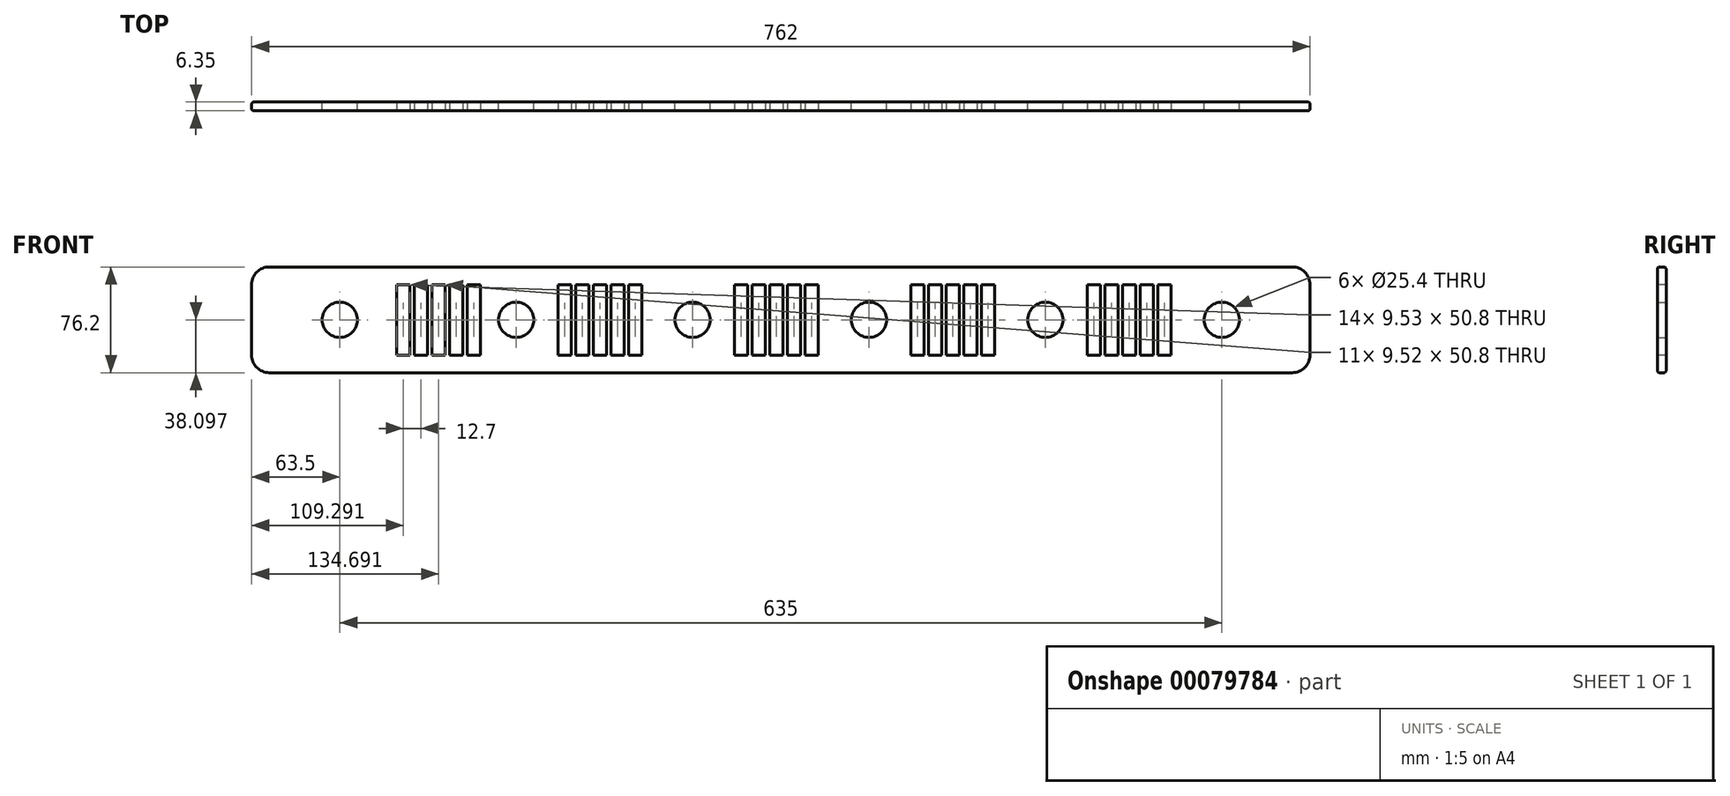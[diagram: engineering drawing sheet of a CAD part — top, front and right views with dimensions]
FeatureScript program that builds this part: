
annotation { "Feature Type Name" : "Feature", "Feature Type Description" : "" }
export const myFeature = defineFeature(function(context is Context, id is Id, definition is map)
    precondition{}
    {
        {
            var Q0;
            Q0=qCreatedBy(makeId("Front.planeOp"),FACE);
            var sketch = newSketch(context, id + "F0", { "sketchPlane" : qUnion([Q0])});
            skLineSegment(sketch, "E0.bottom", {"start": v(-190.5, 22.29) * mm, "end": v(571.5, 22.29) * mm});
            skLineSegment(sketch, "E0.top", {"start": v(-190.5, -53.91) * mm, "end": v(571.5, -53.91) * mm});
            skLineSegment(sketch, "E0.left", {"start": v(-190.5, 22.29) * mm, "end": v(-190.5, -53.91) * mm});
            skLineSegment(sketch, "E0.right", {"start": v(571.5, 22.29) * mm, "end": v(571.5, -53.91) * mm});
            skCircle(sketch, "E1", {"center": v(-127, -15.81) * mm, "radius": 12.7 * mm});
            skPoint(sketch, "E1.centerSnap0", {"position": v(-190.5, -15.81) * mm});
            skCircle(sketch, "E2", {"center": v(0, -15.81) * mm, "radius": 12.7 * mm});
            skCircle(sketch, "E3", {"center": v(127, -15.81) * mm, "radius": 12.7 * mm});
            skCircle(sketch, "E4", {"center": v(254, -15.81) * mm, "radius": 12.7 * mm});
            skCircle(sketch, "E5", {"center": v(381, -15.81) * mm, "radius": 12.7 * mm});
            skCircle(sketch, "E6", {"center": v(508, -15.81) * mm, "radius": 12.7 * mm});
            skSolve(sketch);
        }
        {
            var Q0;
            Q0=makeQuery(id+"F0.imprint","IMPRINT",FACE,{"disambiguationData":[TD([[makeQuery(id+"F0.imprint","IMPRINT",EDGE,{"derivedFrom":sQuery(id+"F0.wireOp",EDGE,"E0.bottom")}),-1.0]])]});
            extrude(context, id + "F1", {"entities" : qUnion([Q0]), "depth" : 6.35 * mm});
        }
        {
            var Q0;
            Q0=makeQuery(id+"F1.opExtrude","CAP_FACE",FACE,{"disambiguationData":[OSD([sQuery(id+"F0.wireOp",EDGE,"E0.bottom"),sQuery(id+"F0.wireOp",EDGE,"E0.top"),sQuery(id+"F0.wireOp",EDGE,"E0.left"),sQuery(id+"F0.wireOp",EDGE,"E0.right"),sQuery(id+"F0.wireOp",EDGE,"E1"),sQuery(id+"F0.wireOp",EDGE,"E2"),sQuery(id+"F0.wireOp",EDGE,"E3"),sQuery(id+"F0.wireOp",EDGE,"E4"),sQuery(id+"F0.wireOp",EDGE,"E5"),sQuery(id+"F0.wireOp",EDGE,"E6")])],"isStart":false});
            var sketch = newSketch(context, id + "F2", { "sketchPlane" : qUnion([Q0])});
            skLineSegment(sketch, "E7.bottom", {"start": v(30.18, 9.59) * mm, "end": v(39.7, 9.59) * mm});
            skLineSegment(sketch, "E7.top", {"start": v(30.18, -41.21) * mm, "end": v(39.7, -41.21) * mm});
            skLineSegment(sketch, "E7.left", {"start": v(30.18, 9.59) * mm, "end": v(30.18, -41.21) * mm});
            skLineSegment(sketch, "E7.right", {"start": v(39.7, 9.59) * mm, "end": v(39.7, -41.21) * mm});
            skLineSegment(sketch, "E8.1.0.0", {"start": v(42.88, 9.59) * mm, "end": v(42.88, -41.21) * mm});
            skLineSegment(sketch, "E8.1.0.1", {"start": v(52.4, 9.59) * mm, "end": v(52.4, -41.21) * mm});
            skLineSegment(sketch, "E8.1.0.2", {"start": v(42.88, -41.21) * mm, "end": v(52.4, -41.21) * mm});
            skLineSegment(sketch, "E8.1.0.3", {"start": v(42.88, 9.59) * mm, "end": v(52.4, 9.59) * mm});
            skLineSegment(sketch, "E8.2.0.0", {"start": v(55.58, 9.59) * mm, "end": v(55.58, -41.21) * mm});
            skLineSegment(sketch, "E8.2.0.1", {"start": v(65.1, 9.59) * mm, "end": v(65.1, -41.21) * mm});
            skLineSegment(sketch, "E8.2.0.2", {"start": v(55.58, -41.21) * mm, "end": v(65.1, -41.21) * mm});
            skLineSegment(sketch, "E8.2.0.3", {"start": v(55.58, 9.59) * mm, "end": v(65.1, 9.59) * mm});
            skLineSegment(sketch, "E8.3.0.0", {"start": v(68.28, 9.59) * mm, "end": v(68.28, -41.21) * mm});
            skLineSegment(sketch, "E8.3.0.1", {"start": v(77.8, 9.59) * mm, "end": v(77.8, -41.21) * mm});
            skLineSegment(sketch, "E8.3.0.2", {"start": v(68.28, -41.21) * mm, "end": v(77.8, -41.21) * mm});
            skLineSegment(sketch, "E8.3.0.3", {"start": v(68.28, 9.59) * mm, "end": v(77.8, 9.59) * mm});
            skLineSegment(sketch, "E8.4.0.0", {"start": v(80.98, 9.59) * mm, "end": v(80.98, -41.21) * mm});
            skLineSegment(sketch, "E8.4.0.1", {"start": v(90.5, 9.59) * mm, "end": v(90.5, -41.21) * mm});
            skLineSegment(sketch, "E8.4.0.2", {"start": v(80.98, -41.21) * mm, "end": v(90.5, -41.21) * mm});
            skLineSegment(sketch, "E8.4.0.3", {"start": v(80.98, 9.59) * mm, "end": v(90.5, 9.59) * mm});
            skLineSegment(sketch, "E8.direction1", {"start": v(30.18, -41.21) * mm, "end": v(42.88, -41.21) * mm, "construction": true});
            skLineSegment(sketch, "E9.bottom", {"start": v(157.18, 9.59) * mm, "end": v(166.7, 9.59) * mm});
            skLineSegment(sketch, "E9.top", {"start": v(157.18, -41.21) * mm, "end": v(166.7, -41.21) * mm});
            skLineSegment(sketch, "E9.left", {"start": v(157.18, 9.59) * mm, "end": v(157.18, -41.21) * mm});
            skLineSegment(sketch, "E9.right", {"start": v(166.7, 9.59) * mm, "end": v(166.7, -41.21) * mm});
            skLineSegment(sketch, "E10.1.0.0", {"start": v(169.88, 9.59) * mm, "end": v(169.88, -41.21) * mm});
            skLineSegment(sketch, "E10.1.0.1", {"start": v(179.4, 9.59) * mm, "end": v(179.4, -41.21) * mm});
            skLineSegment(sketch, "E10.1.0.2", {"start": v(169.88, -41.21) * mm, "end": v(179.4, -41.21) * mm});
            skLineSegment(sketch, "E10.1.0.3", {"start": v(169.88, 9.59) * mm, "end": v(179.4, 9.59) * mm});
            skLineSegment(sketch, "E10.2.0.0", {"start": v(182.58, 9.59) * mm, "end": v(182.58, -41.21) * mm});
            skLineSegment(sketch, "E10.2.0.1", {"start": v(192.1, 9.59) * mm, "end": v(192.1, -41.21) * mm});
            skLineSegment(sketch, "E10.2.0.2", {"start": v(182.58, -41.21) * mm, "end": v(192.1, -41.21) * mm});
            skLineSegment(sketch, "E10.2.0.3", {"start": v(182.58, 9.59) * mm, "end": v(192.1, 9.59) * mm});
            skLineSegment(sketch, "E10.3.0.0", {"start": v(195.28, 9.59) * mm, "end": v(195.28, -41.21) * mm});
            skLineSegment(sketch, "E10.3.0.1", {"start": v(204.8, 9.59) * mm, "end": v(204.8, -41.21) * mm});
            skLineSegment(sketch, "E10.3.0.2", {"start": v(195.28, -41.21) * mm, "end": v(204.8, -41.21) * mm});
            skLineSegment(sketch, "E10.3.0.3", {"start": v(195.28, 9.59) * mm, "end": v(204.8, 9.59) * mm});
            skLineSegment(sketch, "E10.4.0.0", {"start": v(207.98, 9.59) * mm, "end": v(207.98, -41.21) * mm});
            skLineSegment(sketch, "E10.4.0.1", {"start": v(217.5, 9.59) * mm, "end": v(217.5, -41.21) * mm});
            skLineSegment(sketch, "E10.4.0.2", {"start": v(207.98, -41.21) * mm, "end": v(217.5, -41.21) * mm});
            skLineSegment(sketch, "E10.4.0.3", {"start": v(207.98, 9.59) * mm, "end": v(217.5, 9.59) * mm});
            skLineSegment(sketch, "E10.direction1", {"start": v(157.18, -41.21) * mm, "end": v(169.88, -41.21) * mm, "construction": true});
            skLineSegment(sketch, "E11.bottom", {"start": v(284.18, 9.59) * mm, "end": v(293.7, 9.59) * mm});
            skLineSegment(sketch, "E11.top", {"start": v(284.18, -41.21) * mm, "end": v(293.7, -41.21) * mm});
            skLineSegment(sketch, "E11.left", {"start": v(284.18, 9.59) * mm, "end": v(284.18, -41.21) * mm});
            skLineSegment(sketch, "E11.right", {"start": v(293.7, 9.59) * mm, "end": v(293.7, -41.21) * mm});
            skLineSegment(sketch, "E12.1.0.0", {"start": v(296.88, 9.59) * mm, "end": v(296.88, -41.21) * mm});
            skLineSegment(sketch, "E12.1.0.1", {"start": v(306.4, 9.59) * mm, "end": v(306.4, -41.21) * mm});
            skLineSegment(sketch, "E12.1.0.2", {"start": v(296.88, -41.21) * mm, "end": v(306.4, -41.21) * mm});
            skLineSegment(sketch, "E12.1.0.3", {"start": v(296.88, 9.59) * mm, "end": v(306.4, 9.59) * mm});
            skLineSegment(sketch, "E12.2.0.0", {"start": v(309.58, 9.59) * mm, "end": v(309.58, -41.21) * mm});
            skLineSegment(sketch, "E12.2.0.1", {"start": v(319.1, 9.59) * mm, "end": v(319.1, -41.21) * mm});
            skLineSegment(sketch, "E12.2.0.2", {"start": v(309.58, -41.21) * mm, "end": v(319.1, -41.21) * mm});
            skLineSegment(sketch, "E12.2.0.3", {"start": v(309.58, 9.59) * mm, "end": v(319.1, 9.59) * mm});
            skLineSegment(sketch, "E12.3.0.0", {"start": v(322.28, 9.59) * mm, "end": v(322.28, -41.21) * mm});
            skLineSegment(sketch, "E12.3.0.1", {"start": v(331.8, 9.59) * mm, "end": v(331.8, -41.21) * mm});
            skLineSegment(sketch, "E12.3.0.2", {"start": v(322.28, -41.21) * mm, "end": v(331.8, -41.21) * mm});
            skLineSegment(sketch, "E12.3.0.3", {"start": v(322.28, 9.59) * mm, "end": v(331.8, 9.59) * mm});
            skLineSegment(sketch, "E12.4.0.0", {"start": v(334.98, 9.59) * mm, "end": v(334.98, -41.21) * mm});
            skLineSegment(sketch, "E12.4.0.1", {"start": v(344.5, 9.59) * mm, "end": v(344.5, -41.21) * mm});
            skLineSegment(sketch, "E12.4.0.2", {"start": v(334.98, -41.21) * mm, "end": v(344.5, -41.21) * mm});
            skLineSegment(sketch, "E12.4.0.3", {"start": v(334.98, 9.59) * mm, "end": v(344.5, 9.59) * mm});
            skLineSegment(sketch, "E12.direction1", {"start": v(284.18, -41.21) * mm, "end": v(296.88, -41.21) * mm, "construction": true});
            skLineSegment(sketch, "E13.bottom", {"start": v(411.18, 9.59) * mm, "end": v(420.7, 9.59) * mm});
            skLineSegment(sketch, "E13.top", {"start": v(411.18, -41.21) * mm, "end": v(420.7, -41.21) * mm});
            skLineSegment(sketch, "E13.left", {"start": v(411.18, 9.59) * mm, "end": v(411.18, -41.21) * mm});
            skLineSegment(sketch, "E13.right", {"start": v(420.7, 9.59) * mm, "end": v(420.7, -41.21) * mm});
            skLineSegment(sketch, "E14.1.0.0", {"start": v(423.88, 9.59) * mm, "end": v(423.88, -41.21) * mm});
            skLineSegment(sketch, "E14.1.0.1", {"start": v(433.4, 9.59) * mm, "end": v(433.4, -41.21) * mm});
            skLineSegment(sketch, "E14.1.0.2", {"start": v(423.88, -41.21) * mm, "end": v(433.4, -41.21) * mm});
            skLineSegment(sketch, "E14.1.0.3", {"start": v(423.88, 9.59) * mm, "end": v(433.4, 9.59) * mm});
            skLineSegment(sketch, "E14.2.0.0", {"start": v(436.58, 9.59) * mm, "end": v(436.58, -41.21) * mm});
            skLineSegment(sketch, "E14.2.0.1", {"start": v(446.1, 9.59) * mm, "end": v(446.1, -41.21) * mm});
            skLineSegment(sketch, "E14.2.0.2", {"start": v(436.58, -41.21) * mm, "end": v(446.1, -41.21) * mm});
            skLineSegment(sketch, "E14.2.0.3", {"start": v(436.58, 9.59) * mm, "end": v(446.1, 9.59) * mm});
            skLineSegment(sketch, "E14.3.0.0", {"start": v(449.28, 9.59) * mm, "end": v(449.28, -41.21) * mm});
            skLineSegment(sketch, "E14.3.0.1", {"start": v(458.8, 9.59) * mm, "end": v(458.8, -41.21) * mm});
            skLineSegment(sketch, "E14.3.0.2", {"start": v(449.28, -41.21) * mm, "end": v(458.8, -41.21) * mm});
            skLineSegment(sketch, "E14.3.0.3", {"start": v(449.28, 9.59) * mm, "end": v(458.8, 9.59) * mm});
            skLineSegment(sketch, "E14.4.0.0", {"start": v(461.98, 9.59) * mm, "end": v(461.98, -41.21) * mm});
            skLineSegment(sketch, "E14.4.0.1", {"start": v(471.5, 9.59) * mm, "end": v(471.5, -41.21) * mm});
            skLineSegment(sketch, "E14.4.0.2", {"start": v(461.98, -41.21) * mm, "end": v(471.5, -41.21) * mm});
            skLineSegment(sketch, "E14.4.0.3", {"start": v(461.98, 9.59) * mm, "end": v(471.5, 9.59) * mm});
            skLineSegment(sketch, "E14.direction1", {"start": v(411.18, -41.21) * mm, "end": v(423.88, -41.21) * mm, "construction": true});
            skLineSegment(sketch, "E15.bottom", {"start": v(-85.97, 9.59) * mm, "end": v(-76.45, 9.59) * mm});
            skLineSegment(sketch, "E15.top", {"start": v(-85.97, -41.21) * mm, "end": v(-76.45, -41.21) * mm});
            skLineSegment(sketch, "E15.left", {"start": v(-85.97, 9.59) * mm, "end": v(-85.97, -41.21) * mm});
            skLineSegment(sketch, "E15.right", {"start": v(-76.45, 9.59) * mm, "end": v(-76.45, -41.21) * mm});
            skLineSegment(sketch, "E16.1.0.0", {"start": v(-73.27, 9.59) * mm, "end": v(-73.27, -41.21) * mm});
            skLineSegment(sketch, "E16.1.0.1", {"start": v(-63.75, 9.59) * mm, "end": v(-63.75, -41.21) * mm});
            skLineSegment(sketch, "E16.1.0.2", {"start": v(-73.27, -41.21) * mm, "end": v(-63.75, -41.21) * mm});
            skLineSegment(sketch, "E16.1.0.3", {"start": v(-73.27, 9.59) * mm, "end": v(-63.75, 9.59) * mm});
            skLineSegment(sketch, "E16.2.0.0", {"start": v(-60.57, 9.59) * mm, "end": v(-60.57, -41.21) * mm});
            skLineSegment(sketch, "E16.2.0.1", {"start": v(-51.05, 9.59) * mm, "end": v(-51.05, -41.21) * mm});
            skLineSegment(sketch, "E16.2.0.2", {"start": v(-60.57, -41.21) * mm, "end": v(-51.05, -41.21) * mm});
            skLineSegment(sketch, "E16.2.0.3", {"start": v(-60.57, 9.59) * mm, "end": v(-51.05, 9.59) * mm});
            skLineSegment(sketch, "E16.3.0.0", {"start": v(-47.87, 9.59) * mm, "end": v(-47.87, -41.21) * mm});
            skLineSegment(sketch, "E16.3.0.1", {"start": v(-38.35, 9.59) * mm, "end": v(-38.35, -41.21) * mm});
            skLineSegment(sketch, "E16.3.0.2", {"start": v(-47.87, -41.21) * mm, "end": v(-38.35, -41.21) * mm});
            skLineSegment(sketch, "E16.3.0.3", {"start": v(-47.87, 9.59) * mm, "end": v(-38.35, 9.59) * mm});
            skLineSegment(sketch, "E16.4.0.0", {"start": v(-35.17, 9.59) * mm, "end": v(-35.17, -41.21) * mm});
            skLineSegment(sketch, "E16.4.0.1", {"start": v(-25.65, 9.59) * mm, "end": v(-25.65, -41.21) * mm});
            skLineSegment(sketch, "E16.4.0.2", {"start": v(-35.17, -41.21) * mm, "end": v(-25.65, -41.21) * mm});
            skLineSegment(sketch, "E16.4.0.3", {"start": v(-35.17, 9.59) * mm, "end": v(-25.65, 9.59) * mm});
            skLineSegment(sketch, "E16.direction1", {"start": v(-85.97, -41.21) * mm, "end": v(-73.27, -41.21) * mm, "construction": true});
            skSolve(sketch);
        }
        {
            var Q0;
            Q0 = qSketchRegion(id + "F2", true);
            extrude(context, id + "F3", {"entities" : qUnion([Q0]), "operationType" : NewBodyOperationType.REMOVE, "oppositeDirection" : true, "depth" : 25.4 * mm});
        }
        {
            var Q0;
            Q0=makeQuery(id+"F1.opExtrude","SWEPT_EDGE",EDGE,{"disambiguationData":[OSD([sQuery(id+"F0.wireOp",EDGE,"E0.bottom"),sQuery(id+"F0.wireOp",EDGE,"E0.left")])]});
            var Q1;
            Q1=makeQuery(id+"F1.opExtrude","SWEPT_EDGE",EDGE,{"disambiguationData":[OSD([sQuery(id+"F0.wireOp",EDGE,"E0.top"),sQuery(id+"F0.wireOp",EDGE,"E0.left")])]});
            var Q2;
            Q2=makeQuery(id+"F1.opExtrude","SWEPT_EDGE",EDGE,{"disambiguationData":[OSD([sQuery(id+"F0.wireOp",EDGE,"E0.bottom"),sQuery(id+"F0.wireOp",EDGE,"E0.right")])]});
            var Q3;
            Q3=makeQuery(id+"F1.opExtrude","SWEPT_EDGE",EDGE,{"disambiguationData":[OSD([sQuery(id+"F0.wireOp",EDGE,"E0.top"),sQuery(id+"F0.wireOp",EDGE,"E0.right")])]});
            fillet(context, id + "F4", {"entities" : qUnion([Q0, Q1, Q2, Q3]), "radius" : 12.7 * mm, "tangentPropagation" : true, "allowEdgeOverflow" : false});
        }
        {
            var Q0;
            Q0=makeQuery(id+"F1.opExtrude","CAP_EDGE",EDGE,{"disambiguationData":[OSD([sQuery(id+"F0.wireOp",EDGE,"E0.bottom")])],"isStart":false});
            var Q1;
            Q1=makeQuery(id+"F1.opExtrude","CAP_EDGE",EDGE,{"disambiguationData":[OSD([sQuery(id+"F0.wireOp",EDGE,"E0.bottom")])],"isStart":true});
            fillet(context, id + "F5", {"entities" : qUnion([Q0, Q1]), "radius" : 1.6 * mm, "tangentPropagation" : true, "allowEdgeOverflow" : false});
        }
    });
